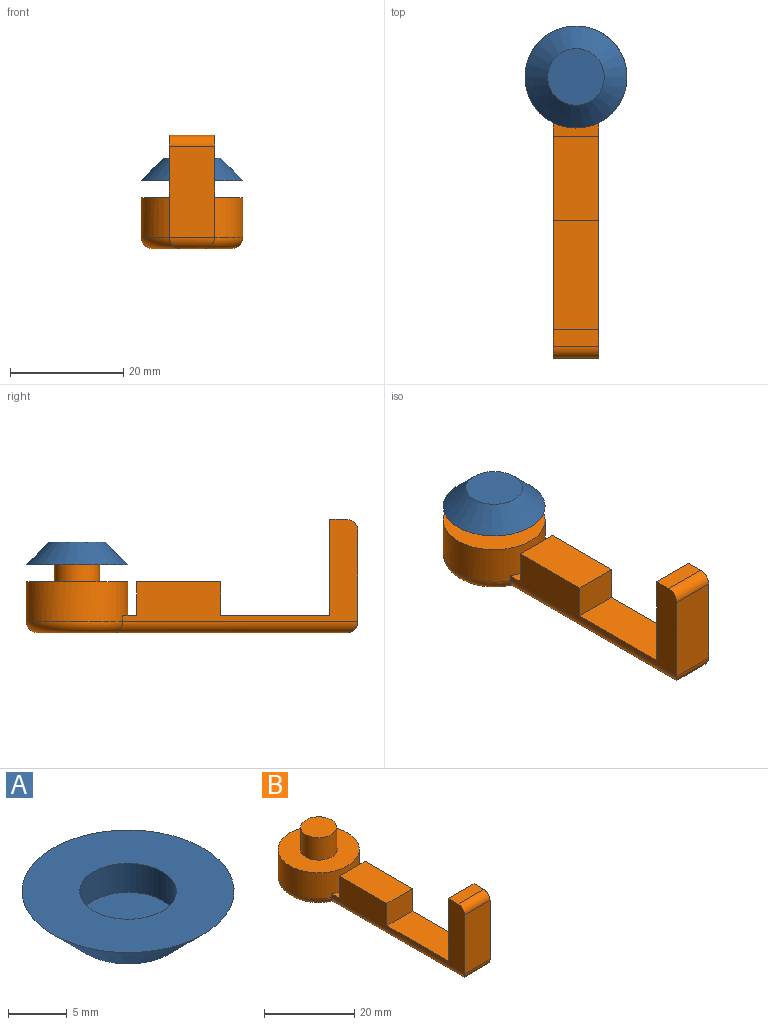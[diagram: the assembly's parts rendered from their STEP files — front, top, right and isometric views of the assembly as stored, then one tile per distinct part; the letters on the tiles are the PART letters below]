
ASSEMBLY  parts=2 mates=1
PART A: 5 faces, bbox 18x18x4 mm
  f0: cylinder r=4.1mm len=8.2mm, axis (0,0,-1), area 77.3mm2, adj f1,f3
  f1: plane 18x18mm, normal (0,0,1), area 201.7mm2, adj f0,f4
  f2: plane 10x10mm, normal (0,0,-1), area 78.5mm2, adj f4
  f3: plane 8.2x8.2mm, normal (0,0,1), area 52.8mm2, adj f0
  f4: cone r=9mm half-angle=45deg, axis (0,0,1), area 248.8mm2, adj f1,f2
PART B: 24 faces, bbox 19.5x59.3x20 mm
  f0: plane 8x2.45mm, normal (0,0,1), area 14.5mm2, adj f4,f5,f6,f15
  f1: plane 8x4.1mm, normal (0,0,1), area 1.2mm2, adj f2,f3,f7,f13
  f2: cylinder r=4.1mm len=9mm, axis (0,0,-1), area 198.7mm2, adj f1,f3,f7,f9,f18
  f3: plane 3x0.9mm, normal (1,0,0), area 2.7mm2, adj f1,f2,f9,f13
  f4: cylinder r=9mm len=18mm, axis (0,0,-1), area 387.6mm2, adj f0,f5,f6,f18,f19
  f5: plane 41.54x18mm, normal (-1,0,0), area 214.7mm2, adj f0,f4,f8,f10,f11,f12,f15,f16
  f6: plane 41.54x18mm, normal (1,0,0), area 214.7mm2, adj f0,f4,f8,f10,f11,f12,f15,f16
  f7: plane 3x0.9mm, normal (-1,0,0), area 2.7mm2, adj f1,f2,f9,f13
  f8: plane 19.26x8mm, normal (0,0,1), area 154.1mm2, adj f5,f6,f10,f16
  f9: plane 54.6x14mm, normal (0,0,-1), area 315.3mm2, adj f2,f3,f7,f13,f19,f20,f21,f22
  f10: plane 17x8mm, normal (0,1,0), area 136mm2, adj f5,f6,f8,f12
  f11: plane 16x8mm, normal (0,-1,0), area 128mm2, adj f5,f6,f22,f23
  f12: plane 8x3mm, normal (0,0,1), area 24mm2, adj f5,f6,f10,f23
  f13: cylinder r=4mm len=15mm, axis (0,0,-1), area 339.3mm2, adj f1,f3,f7,f9,f14
  f14: plane 8x8mm, normal (0,0,1), area 50.3mm2, adj f13
  f15: plane 8x6mm, normal (0,1,0), area 48mm2, adj f0,f5,f6,f17
  f16: plane 8x6mm, normal (0,-1,0), area 48mm2, adj f5,f6,f8,f17
  f17: plane 14.83x8mm, normal (0,0,1), area 118.7mm2, adj f5,f6,f15,f16
  f18: plane 18x18mm, normal (0,0,1), area 201.7mm2, adj f2,f4
  f19: torus R=7mm, axis (0,0,1), area 142.1mm2, adj f4,f9,f20,f21
  f20: cylinder r=2mm len=42.89mm, axis (0,-1,0), area 129.7mm2, adj f5,f9,f19,f22
  f21: cylinder r=2mm len=42.89mm, axis (0,1,0), area 129.7mm2, adj f6,f9,f19,f22
  f22: cylinder r=2mm len=8mm, axis (1,0,0), area 20.6mm2, adj f9,f11,f20,f21
  f23: cylinder r=2mm len=8mm, axis (-1,0,0), area 25.1mm2, adj f5,f6,f11,f12
PLACE A rot(axis=(0,1,0),180deg) t=(0,0,13)mm
PLACE B t=(0,0,-3)mm
MATE fastened A.f0 <-> B.f13  axis (0,0,-1) through (0,0,12)mm
